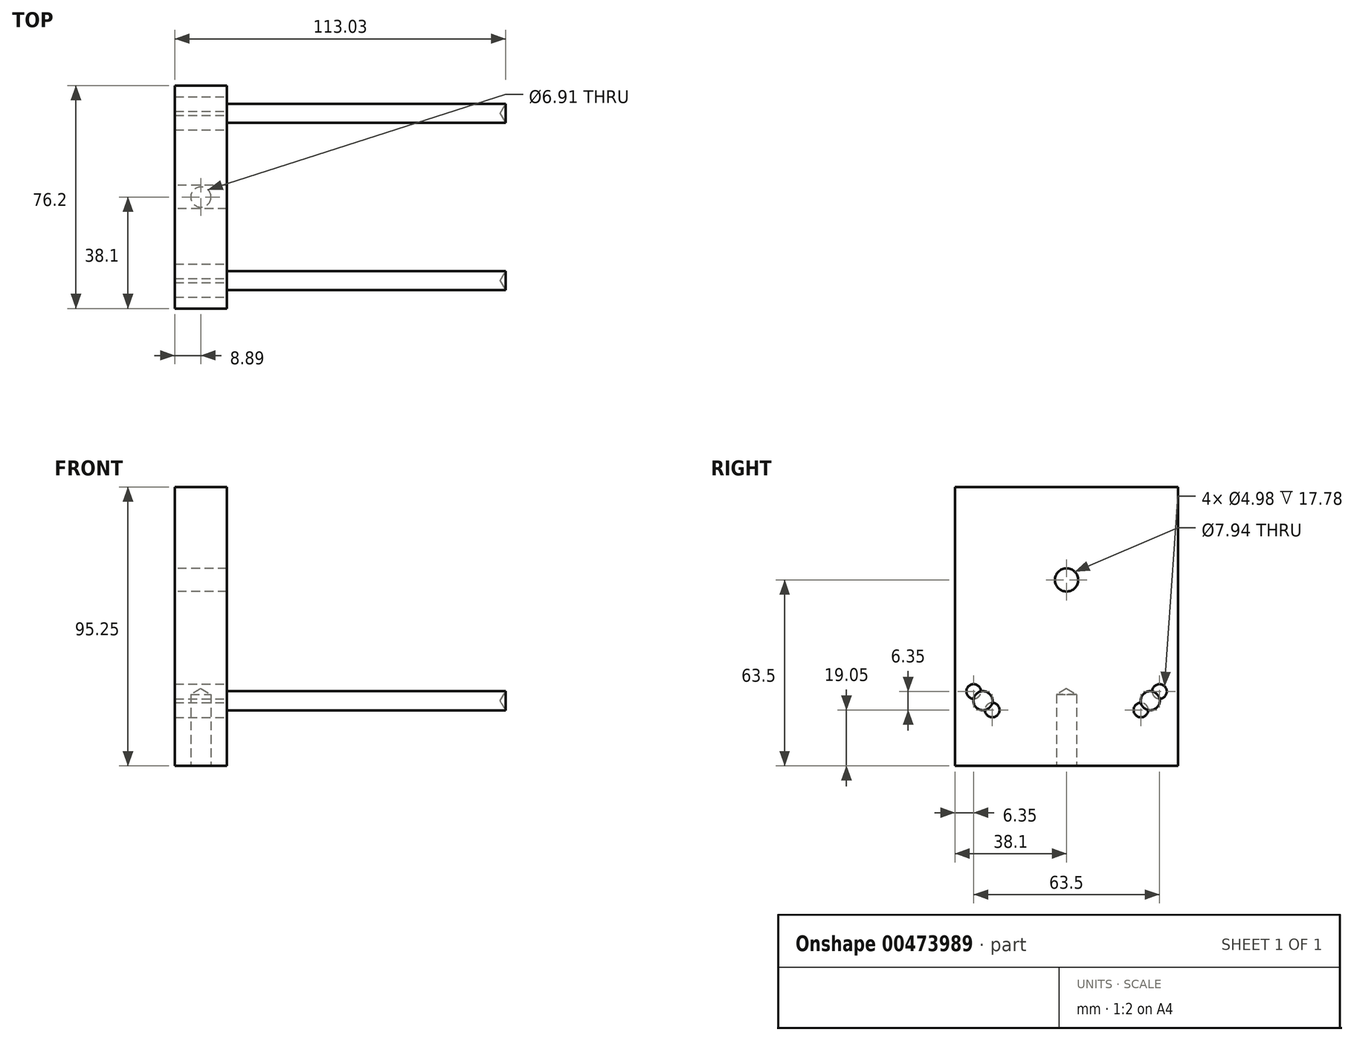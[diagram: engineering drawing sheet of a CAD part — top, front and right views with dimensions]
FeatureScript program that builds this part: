
annotation { "Feature Type Name" : "Feature", "Feature Type Description" : "" }
export const myFeature = defineFeature(function(context is Context, id is Id, definition is map)
    precondition{}
    {
        {
            var Q0;
            Q0=qCreatedBy(makeId("Top.planeOp"),FACE);
            var sketch = newSketch(context, id + "F0", { "sketchPlane" : qUnion([Q0])});
            skLineSegment(sketch, "E0.bottom", {"start": v(0, 0) * mm, "end": v(177.8, 0) * mm});
            skLineSegment(sketch, "E0.top", {"start": v(0, 76.2) * mm, "end": v(177.8, 76.2) * mm});
            skLineSegment(sketch, "E0.left", {"start": v(0, 0) * mm, "end": v(0, 76.2) * mm});
            skLineSegment(sketch, "E0.right", {"start": v(177.8, 0) * mm, "end": v(177.8, 76.2) * mm});
            skSolve(sketch);
        }
        {
            var Q0;
            Q0 = qSketchRegion(id + "F0", true);
            extrude(context, id + "F1", {"entities" : qUnion([Q0]), "depth" : 31.75 * mm});
        }
        {
            var Q0;
            Q0=makeQuery(id+"F1.opExtrude","CAP_FACE",FACE,{"disambiguationData":[OSD([sQuery(id+"F0.wireOp",EDGE,"E0.bottom"),sQuery(id+"F0.wireOp",EDGE,"E0.top"),sQuery(id+"F0.wireOp",EDGE,"E0.left"),sQuery(id+"F0.wireOp",EDGE,"E0.right")])],"isStart":false});
            var sketch = newSketch(context, id + "F2", { "sketchPlane" : qUnion([Q0])});
            skLineSegment(sketch, "E1.bottom", {"start": v(0, 76.2) * mm, "end": v(19.05, 76.2) * mm});
            skLineSegment(sketch, "E1.top", {"start": v(0, 0) * mm, "end": v(19.05, 0) * mm});
            skLineSegment(sketch, "E1.left", {"start": v(0, 76.2) * mm, "end": v(0, 0) * mm});
            skLineSegment(sketch, "E1.right", {"start": v(19.05, 76.2) * mm, "end": v(19.05, 0) * mm});
            skLineSegment(sketch, "E2.bottom", {"start": v(133.35, 76.2) * mm, "end": v(177.8, 76.2) * mm});
            skLineSegment(sketch, "E2.top", {"start": v(133.35, 0) * mm, "end": v(177.8, 0) * mm});
            skLineSegment(sketch, "E2.left", {"start": v(133.35, 76.2) * mm, "end": v(133.35, 0) * mm});
            skLineSegment(sketch, "E2.right", {"start": v(177.8, 76.2) * mm, "end": v(177.8, 0) * mm});
            skSolve(sketch);
        }
        {
            var Q0;
            Q0=makeQuery(id+"F2.imprint","IMPRINT",FACE,{"disambiguationData":[TD([[makeQuery(id+"F2.imprint","IMPRINT",EDGE,{"derivedFrom":sQuery(id+"F2.wireOp",EDGE,"E1.bottom")}),-1.0]])]});
            extrude(context, id + "F3", {"entities" : qUnion([Q0]), "operationType" : NewBodyOperationType.ADD, "depth" : 63.5 * mm});
        }
        {
            var Q0;
            Q0=makeQuery(id+"F1.opExtrude","CAP_FACE",FACE,{"disambiguationData":[OSD([sQuery(id+"F0.wireOp",EDGE,"E0.bottom"),sQuery(id+"F0.wireOp",EDGE,"E0.top"),sQuery(id+"F0.wireOp",EDGE,"E0.left"),sQuery(id+"F0.wireOp",EDGE,"E0.right")])],"isStart":false});
            var sketch = newSketch(context, id + "F4", { "sketchPlane" : qUnion([Q0])});
            skLineSegment(sketch, "E3.bottom", {"start": v(19.05, 57.15) * mm, "end": v(127, 57.15) * mm});
            skLineSegment(sketch, "E3.top", {"start": v(19.05, 19.05) * mm, "end": v(127, 19.05) * mm});
            skLineSegment(sketch, "E3.left", {"start": v(19.05, 57.15) * mm, "end": v(19.05, 19.05) * mm});
            skLineSegment(sketch, "E3.right", {"start": v(127, 57.15) * mm, "end": v(127, 19.05) * mm});
            skSolve(sketch);
        }
        {
            var Q0;
            Q0=makeQuery(id+"F4.imprint","IMPRINT",FACE,{"disambiguationData":[TD([[makeQuery(id+"F4.imprint","IMPRINT",EDGE,{"derivedFrom":sQuery(id+"F4.wireOp",EDGE,"E3.bottom")}),-1.0]])]});
            extrude(context, id + "F5", {"entities" : qUnion([Q0]), "operationType" : NewBodyOperationType.REMOVE, "endBound" : BoundingType.THROUGH_ALL, "oppositeDirection" : true, "depth" : 25.4 * mm});
        }
        {
            var Q0;
            Q0=makeQuery(id+"F1.opExtrude","CAP_FACE",FACE,{"disambiguationData":[OSD([sQuery(id+"F0.wireOp",EDGE,"E0.bottom"),sQuery(id+"F0.wireOp",EDGE,"E0.top"),sQuery(id+"F0.wireOp",EDGE,"E0.left"),sQuery(id+"F0.wireOp",EDGE,"E0.right")])],"isStart":true});
            var sketch = newSketch(context, id + "F6", { "sketchPlane" : qUnion([Q0])});
            skLineSegment(sketch, "E4", {"start": v(19.05, -19.05) * mm, "end": v(19.05, 0) * mm});
            skLineSegment(sketch, "E5", {"start": v(127, -19.05) * mm, "end": v(127, 0) * mm});
            skLineSegment(sketch, "E6", {"start": v(19.05, -57.15) * mm, "end": v(19.05, -76.2) * mm});
            skLineSegment(sketch, "E7", {"start": v(127, -57.15) * mm, "end": v(127, -76.2) * mm});
            skSolve(sketch);
        }
        {
            var Q0;
            Q0 = qSketchRegion(id + "F6", true);
            var Q1;
            {var subQ0=sQuery(id+"F6.wireOp",EDGE,"E4");Q1=makeQuery(id+"F6.imprint","IMPRINT",FACE,{"disambiguationData":[TD([[makeQuery(id+"F6.imprint","IMPRINT",EDGE,{"derivedFrom":subQ0}),-1.0]])]});}
            var Q2;
            {var subQ0=sQuery(id+"F6.wireOp",EDGE,"E6");Q2=makeQuery(id+"F6.imprint","IMPRINT",FACE,{"disambiguationData":[TD([[makeQuery(id+"F6.imprint","IMPRINT",EDGE,{"derivedFrom":subQ0}),1.0]])]});}
            extrude(context, id + "F7", {"entities" : qUnion([Q0, Q1, Q2]), "operationType" : NewBodyOperationType.REMOVE, "oppositeDirection" : true, "depth" : 12.7 * mm});
        }
        {
            var Q0;
            Q0=makeQuery(id+"F1.opExtrude","SWEPT_FACE",FACE,{"disambiguationData":[OSD([sQuery(id+"F0.wireOp",EDGE,"E0.right")])]});
            var sketch = newSketch(context, id + "F8", { "sketchPlane" : qUnion([Q0])});
            skSolve(sketch);
        }
        {
            var Q0;
            Q0 = qSketchRegion(id + "F8", true);
            var Q1;
            {var subQ0=sQuery(id+"F0.wireOp",EDGE,"E0.right");Q1=makeQuery(id+"F8.imprint","IMPRINT",FACE,{"disambiguationData":[TD([[makeQuery(id+"F8.imprint","IMPRINT",EDGE,{"derivedFrom":makeQuery(id+"F1.opExtrude","CAP_EDGE",EDGE,{"disambiguationData":[OSD([subQ0])],"isStart":true})}),1.0]])]});}
            extrude(context, id + "F9", {"entities" : qUnion([Q0, Q1]), "operationType" : NewBodyOperationType.REMOVE, "oppositeDirection" : true, "depth" : 50.8 * mm});
        }
        {
            var Q0;
            {var subQ0=sQuery(id+"F0.wireOp",EDGE,"E0.right");var subQ2=sQuery(id+"F0.wireOp",EDGE,"E0.top");var subQ3=sQuery(id+"F0.wireOp",EDGE,"E0.bottom");Q0=makeQuery(id+"F9.boolean.opBoolean","COPY",FACE,{"disambiguationData":[TD([makeQuery(id+"F1.opExtrude","SWEPT_FACE",FACE,{"disambiguationData":[OSD([subQ3])]})])],"derivedFrom":makeQuery(id+"F9.opExtrude","CAP_FACE",FACE,{"disambiguationData":[OSD([subQ3,subQ2,subQ0])],"isStart":false})});}
            var sketch = newSketch(context, id + "F10", { "sketchPlane" : qUnion([Q0])});
            skPoint(sketch, "E8", {"position": v(9.52, 22.23) * mm});
            skPoint(sketch, "E9", {"position": v(66.67, 22.23) * mm});
            skSolve(sketch);
        }
        {
            var Q0;
            Q0=sQuery(id+"F10.wireOp",VERTEX,"E9");
            var Q1;
            Q1=sQuery(id+"F10.wireOp",VERTEX,"E8");
            var Q2;
            Q2=makeQuery(id+"F1.opExtrude","SWEPT_BODY",BODY,{"disambiguationData":[OSD([sQuery(id+"F0.wireOp",EDGE,"E0.bottom"),sQuery(id+"F0.wireOp",EDGE,"E0.top"),sQuery(id+"F0.wireOp",EDGE,"E0.left"),sQuery(id+"F0.wireOp",EDGE,"E0.right")])]});
            hole(context, id + "F11", {"style" : HoleStyle.SIMPLE, "endStyle" : HoleEndStyle.BLIND, "standardTappedOrClearance" : lookupTablePath({ "standard" : "ANSI", "engagement" : "75%", "pitch" : "18 tpi", "size" : "5/16", "type" : "Tapped" }), "standardBlindInLast" : lookupTablePath({ "standard" : "ANSI", "engagement" : "75%", "pitch" : "18 tpi", "size" : "5/16", "type" : "Tapped" }), "holeDiameter" : 6.53 * mm, "showTappedDepth" : true, "holeDepth" : 12.7 * mm, "isTappedThrough" : true, "tappedDepth" : 8.47 * mm, "tapClearance" : 3, "locations" : qUnion([Q0, Q1]), "scope" : qUnion([Q2]), "majorDiameter" : 7.94 * mm});
        }
        {
            var Q0;
            {var subQ1=sQuery(id+"F0.wireOp",EDGE,"E0.top");var subQ2=sQuery(id+"F0.wireOp",EDGE,"E0.right");var subQ4=sQuery(id+"F0.wireOp",EDGE,"E0.bottom");Q0=makeQuery(id+"F9.boolean.opBoolean","COPY",FACE,{"disambiguationData":[TD([makeQuery(id+"F1.opExtrude","SWEPT_FACE",FACE,{"disambiguationData":[OSD([subQ1])]})])],"derivedFrom":makeQuery(id+"F9.opExtrude","CAP_FACE",FACE,{"disambiguationData":[OSD([subQ4,subQ1,subQ2])],"isStart":false})});}
            var sketch = newSketch(context, id + "F12", { "sketchPlane" : qUnion([Q0])});
            skSolve(sketch);
        }
        {
            var Q0;
            Q0=makeQuery(id+"F3.boolean.opBoolean","MERGE",FACE,{"derivedFrom":[makeQuery(id+"F1.opExtrude","SWEPT_FACE",FACE,{"disambiguationData":[OSD([sQuery(id+"F0.wireOp",EDGE,"E0.left")])]}),makeQuery(id+"F3.opExtrude","SWEPT_FACE",FACE,{"disambiguationData":[OSD([sQuery(id+"F2.wireOp",EDGE,"E1.left")])]})]});
            var sketch = newSketch(context, id + "F13", { "sketchPlane" : qUnion([Q0])});
            skLineSegment(sketch, "E10.0.0", {"start": v(-19.05, 12.7) * mm, "end": v(-19.05, 31.75) * mm});
            skLineSegment(sketch, "E10.0.1", {"start": v(-19.05, 31.75) * mm, "end": v(0, 31.75) * mm});
            skLineSegment(sketch, "E10.0.2", {"start": v(0, 31.75) * mm, "end": v(0, 12.7) * mm});
            skLineSegment(sketch, "E10.0.3", {"start": v(0, 12.7) * mm, "end": v(-19.05, 12.7) * mm});
            skLineSegment(sketch, "E11.0.0", {"start": v(-57.15, 31.75) * mm, "end": v(-57.15, 12.7) * mm});
            skLineSegment(sketch, "E11.0.1", {"start": v(-57.15, 12.7) * mm, "end": v(-76.2, 12.7) * mm});
            skLineSegment(sketch, "E11.0.2", {"start": v(-76.2, 12.7) * mm, "end": v(-76.2, 31.75) * mm});
            skLineSegment(sketch, "E11.0.3", {"start": v(-76.2, 31.75) * mm, "end": v(-57.15, 31.75) * mm});
            skPoint(sketch, "E12", {"position": v(-38.1, 63.5) * mm});
            skSolve(sketch);
        }
        {
            var Q0;
            Q0=sQuery(id+"F13.wireOp",VERTEX,"E12");
            var Q1;
            Q1=makeQuery(id+"F1.opExtrude","SWEPT_BODY",BODY,{"disambiguationData":[OSD([sQuery(id+"F0.wireOp",EDGE,"E0.bottom"),sQuery(id+"F0.wireOp",EDGE,"E0.top"),sQuery(id+"F0.wireOp",EDGE,"E0.left"),sQuery(id+"F0.wireOp",EDGE,"E0.right")])]});
            hole(context, id + "F14", {"style" : HoleStyle.SIMPLE, "endStyle" : HoleEndStyle.THROUGH, "standardTappedOrClearance" : lookupTablePath({ "standard" : "ANSI", "engagement" : "75%", "pitch" : "16 tpi", "size" : "3/8", "type" : "Tapped" }), "standardBlindInLast" : lookupTablePath({ "standard" : "ANSI", "engagement" : "75%", "pitch" : "16 tpi", "size" : "3/8", "type" : "Tapped" }), "holeDiameter" : 7.94 * mm, "showTappedDepth" : true, "isTappedThrough" : true, "tappedDepth" : 8.46 * mm, "tapClearance" : 3, "startFromSketch" : true, "locations" : qUnion([Q0]), "scope" : qUnion([Q1]), "majorDiameter" : 9.53 * mm});
        }
        {
            var Q0;
            {var subQ0=sQuery(id+"F0.wireOp",EDGE,"E0.right");var subQ2=sQuery(id+"F0.wireOp",EDGE,"E0.top");var subQ3=sQuery(id+"F0.wireOp",EDGE,"E0.bottom");Q0=makeQuery(id+"F9.boolean.opBoolean","COPY",FACE,{"disambiguationData":[TD([makeQuery(id+"F1.opExtrude","SWEPT_FACE",FACE,{"disambiguationData":[OSD([subQ3])]})])],"derivedFrom":makeQuery(id+"F9.opExtrude","CAP_FACE",FACE,{"disambiguationData":[OSD([subQ3,subQ2,subQ0])],"isStart":false})});}
            var sketch = newSketch(context, id + "F15", { "sketchPlane" : qUnion([Q0])});
            skCircle(sketch, "E13.0.0", {"center": v(66.67, 22.23) * mm, "radius": 3.26 * mm});
            skLineSegment(sketch, "E13.3.0", {"start": v(57.15, 31.75) * mm, "end": v(57.15, 12.7) * mm});
            skLineSegment(sketch, "E13.3.1", {"start": v(57.15, 12.7) * mm, "end": v(76.2, 12.7) * mm});
            skLineSegment(sketch, "E13.3.2", {"start": v(76.2, 12.7) * mm, "end": v(76.2, 31.75) * mm});
            skLineSegment(sketch, "E13.3.3", {"start": v(76.2, 31.75) * mm, "end": v(57.15, 31.75) * mm});
            skSolve(sketch);
        }
        {
            var Q0;
            Q0 = qSketchRegion(id + "F15", true);
            var Q1;
            Q1=makeQuery(id+"F15.imprint","IMPRINT",FACE,{"disambiguationData":[TD([[makeQuery(id+"F15.imprint","IMPRINT",EDGE,{"derivedFrom":makeQuery(id+"F7.boolean.opBoolean","COPY",EDGE,{"derivedFrom":makeQuery(id+"F7.opExtrude","CAP_EDGE",EDGE,{"disambiguationData":[OSD([sQuery(id+"F6.wireOp",EDGE,"E5")])],"isStart":false})})}),-1.0]])]});
            var Q2;
            Q2=makeQuery(id+"F15.imprint","IMPRINT",FACE,{"disambiguationData":[TD([[makeQuery(id+"F15.imprint","IMPRINT",EDGE,{"derivedFrom":makeQuery(id+"F11.hole-1.boolean.opBoolean","COPY",EDGE,{"derivedFrom":makeQuery(id+"F11.hole-1.opRevolve","SWEPT_EDGE",EDGE,{"disambiguationData":[OSD([sQuery(id+"F11.hole-1.sketch.wireOp",EDGE,"core_line_2"),sQuery(id+"F11.hole-1.sketch.wireOp",EDGE,"core_line_3")])]})})}),1.0]])]});
            var Q3;
            Q3=makeQuery(id+"F12.imprint","IMPRINT",FACE,{"disambiguationData":[TD([[makeQuery(id+"F12.imprint","IMPRINT",EDGE,{"derivedFrom":makeQuery(id+"F11.hole-0.boolean.opBoolean","COPY",EDGE,{"derivedFrom":makeQuery(id+"F11.hole-0.opRevolve","SWEPT_EDGE",EDGE,{"disambiguationData":[OSD([sQuery(id+"F11.hole-0.sketch.wireOp",EDGE,"core_line_2"),sQuery(id+"F11.hole-0.sketch.wireOp",EDGE,"core_line_3")])]})})}),1.0]])]});
            extrude(context, id + "F16", {"entities" : qUnion([Q0, Q1, Q2, Q3]), "operationType" : NewBodyOperationType.REMOVE, "oppositeDirection" : true, "depth" : 107.95 * mm});
        }
        {
            var Q0;
            Q0=makeQuery(id+"F16.boolean.opBoolean","MERGE",FACE,{"derivedFrom":[makeQuery(id+"F7.boolean.opBoolean","MERGE",FACE,{"derivedFrom":[makeQuery(id+"F5.boolean.opBoolean","MERGE",FACE,{"derivedFrom":[makeQuery(id+"F3.opExtrude","SWEPT_FACE",FACE,{"disambiguationData":[OSD([sQuery(id+"F2.wireOp",EDGE,"E1.right")])]}),makeQuery(id+"F5.opExtrude","SWEPT_FACE",FACE,{"disambiguationData":[OSD([sQuery(id+"F4.wireOp",EDGE,"E3.left")])]})]}),makeQuery(id+"F7.opExtrude","SWEPT_FACE",FACE,{"disambiguationData":[OSD([sQuery(id+"F6.wireOp",EDGE,"E4")])]}),makeQuery(id+"F7.opExtrude","SWEPT_FACE",FACE,{"disambiguationData":[OSD([sQuery(id+"F6.wireOp",EDGE,"E6")])]})]}),makeQuery(id+"F16.opExtrude","CAP_FACE",FACE,{"disambiguationData":[OSD([sQuery(id+"F11.hole-0.sketch.wireOp",EDGE,"core_line_2"),sQuery(id+"F11.hole-0.sketch.wireOp",EDGE,"core_line_3")])],"isStart":false}),makeQuery(id+"F16.opExtrude","CAP_FACE",FACE,{"disambiguationData":[OSD([sQuery(id+"F15.wireOp",EDGE,"E13.0.0"),sQuery(id+"F15.wireOp",EDGE,"E13.3.0"),sQuery(id+"F15.wireOp",EDGE,"E13.3.1"),sQuery(id+"F15.wireOp",EDGE,"E13.3.2"),sQuery(id+"F15.wireOp",EDGE,"E13.3.3")])],"isStart":false}),makeQuery(id+"F16.opExtrude","CAP_FACE",FACE,{"disambiguationData":[OSD([sQuery(id+"F0.wireOp",EDGE,"E0.bottom"),sQuery(id+"F0.wireOp",EDGE,"E0.right"),sQuery(id+"F4.wireOp",EDGE,"E3.top"),sQuery(id+"F4.wireOp",EDGE,"E3.right"),sQuery(id+"F6.wireOp",EDGE,"E5")])],"isStart":false})]});
            var sketch = newSketch(context, id + "F17", { "sketchPlane" : qUnion([Q0])});
            skLineSegment(sketch, "E14.bottom", {"start": v(0, 31.75) * mm, "end": v(19.05, 31.75) * mm});
            skLineSegment(sketch, "E14.top", {"start": v(0, 12.7) * mm, "end": v(19.05, 12.7) * mm});
            skLineSegment(sketch, "E14.left", {"start": v(0, 31.75) * mm, "end": v(0, 12.7) * mm});
            skLineSegment(sketch, "E14.right", {"start": v(19.05, 31.75) * mm, "end": v(19.05, 12.7) * mm});
            skLineSegment(sketch, "E15.bottom", {"start": v(76.2, 31.75) * mm, "end": v(57.15, 31.75) * mm});
            skLineSegment(sketch, "E15.top", {"start": v(76.2, 12.7) * mm, "end": v(57.15, 12.7) * mm});
            skLineSegment(sketch, "E15.left", {"start": v(76.2, 31.75) * mm, "end": v(76.2, 12.7) * mm});
            skLineSegment(sketch, "E15.right", {"start": v(57.15, 31.75) * mm, "end": v(57.15, 12.7) * mm});
            skPoint(sketch, "E16", {"position": v(6.35, 25.4) * mm});
            skPoint(sketch, "E17", {"position": v(12.7, 19.05) * mm});
            skPoint(sketch, "E18", {"position": v(69.85, 25.4) * mm});
            skPoint(sketch, "E19", {"position": v(63.5, 19.05) * mm});
            skSolve(sketch);
        }
        {
            var Q0;
            Q0=sQuery(id+"F17.wireOp",VERTEX,"E16");
            var Q1;
            Q1=sQuery(id+"F17.wireOp",VERTEX,"E17");
            var Q2;
            Q2=sQuery(id+"F17.wireOp",VERTEX,"E19");
            var Q3;
            Q3=sQuery(id+"F17.wireOp",VERTEX,"E18");
            var Q4;
            Q4=makeQuery(id+"F1.opExtrude","SWEPT_BODY",BODY,{"disambiguationData":[OSD([sQuery(id+"F0.wireOp",EDGE,"E0.bottom"),sQuery(id+"F0.wireOp",EDGE,"E0.top"),sQuery(id+"F0.wireOp",EDGE,"E0.left"),sQuery(id+"F0.wireOp",EDGE,"E0.right")])]});
            hole(context, id + "F18", {"style" : HoleStyle.SIMPLE, "endStyle" : HoleEndStyle.THROUGH, "standardTappedOrClearance" : lookupTablePath({ "standard" : "ANSI", "fit" : "Close", "size" : "#10", "type" : "Clearance" }), "standardBlindInLast" : lookupTablePath({ "fit" : "Close", "standard" : "ANSI", "size" : "#10", "type" : "Clearance" }), "holeDiameter" : 4.98 * mm, "isTappedThrough" : true, "tappedDepth" : 12.7 * mm, "tapClearance" : 3, "locations" : qUnion([Q0, Q1, Q2, Q3]), "scope" : qUnion([Q4])});
        }
        {
            var Q0;
            Q0=makeQuery(id+"F3.boolean.opBoolean","MERGE",FACE,{"derivedFrom":[makeQuery(id+"F1.opExtrude","SWEPT_FACE",FACE,{"disambiguationData":[OSD([sQuery(id+"F0.wireOp",EDGE,"E0.left")])]}),makeQuery(id+"F3.opExtrude","SWEPT_FACE",FACE,{"disambiguationData":[OSD([sQuery(id+"F2.wireOp",EDGE,"E1.left")])]})]});
            var sketch = newSketch(context, id + "F19", { "sketchPlane" : qUnion([Q0])});
            skLineSegment(sketch, "E20.0.0", {"start": v(-76.2, 0) * mm, "end": v(0, 0) * mm});
            skLineSegment(sketch, "E20.0.1", {"start": v(0, 0) * mm, "end": v(0, 95.25) * mm});
            skLineSegment(sketch, "E20.0.2", {"start": v(0, 95.25) * mm, "end": v(-76.2, 95.25) * mm});
            skLineSegment(sketch, "E20.0.3", {"start": v(-76.2, 95.25) * mm, "end": v(-76.2, 0) * mm});
            skCircle(sketch, "E21.0", {"center": v(-38.1, 63.5) * mm, "radius": 3.97 * mm});
            skCircle(sketch, "E22.0", {"center": v(-69.85, 25.4) * mm, "radius": 2.49 * mm});
            skCircle(sketch, "E23.0", {"center": v(-63.5, 19.05) * mm, "radius": 2.49 * mm});
            skCircle(sketch, "E24.0", {"center": v(-12.7, 19.05) * mm, "radius": 2.49 * mm});
            skCircle(sketch, "E25.0", {"center": v(-6.35, 25.4) * mm, "radius": 2.49 * mm});
            skSolve(sketch);
        }
        {
            var Q0;
            Q0 = qSketchRegion(id + "F19", true);
            extrude(context, id + "F20", {"entities" : qUnion([Q0]), "operationType" : NewBodyOperationType.REMOVE, "oppositeDirection" : true, "depth" : 1.27 * mm});
        }
        {
            var Q0;
            {var subQ0=sQuery(id+"F0.wireOp",EDGE,"E0.left");var subQ1=sQuery(id+"F0.wireOp",EDGE,"E0.top");var subQ2=sQuery(id+"F0.wireOp",EDGE,"E0.bottom");Q0=makeQuery(id+"F7.boolean.opBoolean","SPLIT",FACE,{"disambiguationData":[TD([makeQuery(id+"F1.opExtrude","SWEPT_FACE",FACE,{"disambiguationData":[OSD([subQ0])]})])],"derivedFrom":makeQuery(id+"F1.opExtrude","CAP_FACE",FACE,{"disambiguationData":[OSD([subQ2,subQ1,subQ0,sQuery(id+"F0.wireOp",EDGE,"E0.right")])],"isStart":true})});}
            var sketch = newSketch(context, id + "F21", { "sketchPlane" : qUnion([Q0])});
            skLineSegment(sketch, "E26.0.0", {"start": v(19.05, 0) * mm, "end": v(1.27, 0) * mm});
            skLineSegment(sketch, "E26.0.1", {"start": v(1.27, 0) * mm, "end": v(1.27, -76.2) * mm});
            skLineSegment(sketch, "E26.0.2", {"start": v(1.27, -76.2) * mm, "end": v(19.05, -76.2) * mm});
            skLineSegment(sketch, "E26.0.3", {"start": v(19.05, -76.2) * mm, "end": v(19.05, 0) * mm});
            skPoint(sketch, "E27", {"position": v(10.16, -38.1) * mm});
            skPoint(sketch, "E27.positionSnap0", {"position": v(1.27, -38.1) * mm});
            skSolve(sketch);
        }
        {
            var Q0;
            Q0=sQuery(id+"F21.wireOp",VERTEX,"E27");
            var Q1;
            Q1=makeQuery(id+"F1.opExtrude","SWEPT_BODY",BODY,{"disambiguationData":[OSD([sQuery(id+"F0.wireOp",EDGE,"E0.bottom"),sQuery(id+"F0.wireOp",EDGE,"E0.top"),sQuery(id+"F0.wireOp",EDGE,"E0.left"),sQuery(id+"F0.wireOp",EDGE,"E0.right")])]});
            hole(context, id + "F22", {"style" : HoleStyle.SIMPLE, "endStyle" : HoleEndStyle.BLIND, "standardTappedOrClearance" : lookupTablePath({ "standard" : "ANSI", "engagement" : "75%", "pitch" : "24 tpi", "size" : "5/16", "type" : "Tapped" }), "standardBlindInLast" : lookupTablePath({ "standard" : "ANSI", "engagement" : "75%", "pitch" : "24 tpi", "size" : "5/16", "type" : "Tapped" }), "holeDiameter" : 6.9 * mm, "showTappedDepth" : true, "holeDepth" : 24.34 * mm, "isTappedThrough" : true, "tappedDepth" : 21.17 * mm, "tapClearance" : 3, "locations" : qUnion([Q0]), "scope" : qUnion([Q1]), "majorDiameter" : 7.94 * mm});
        }
    });
